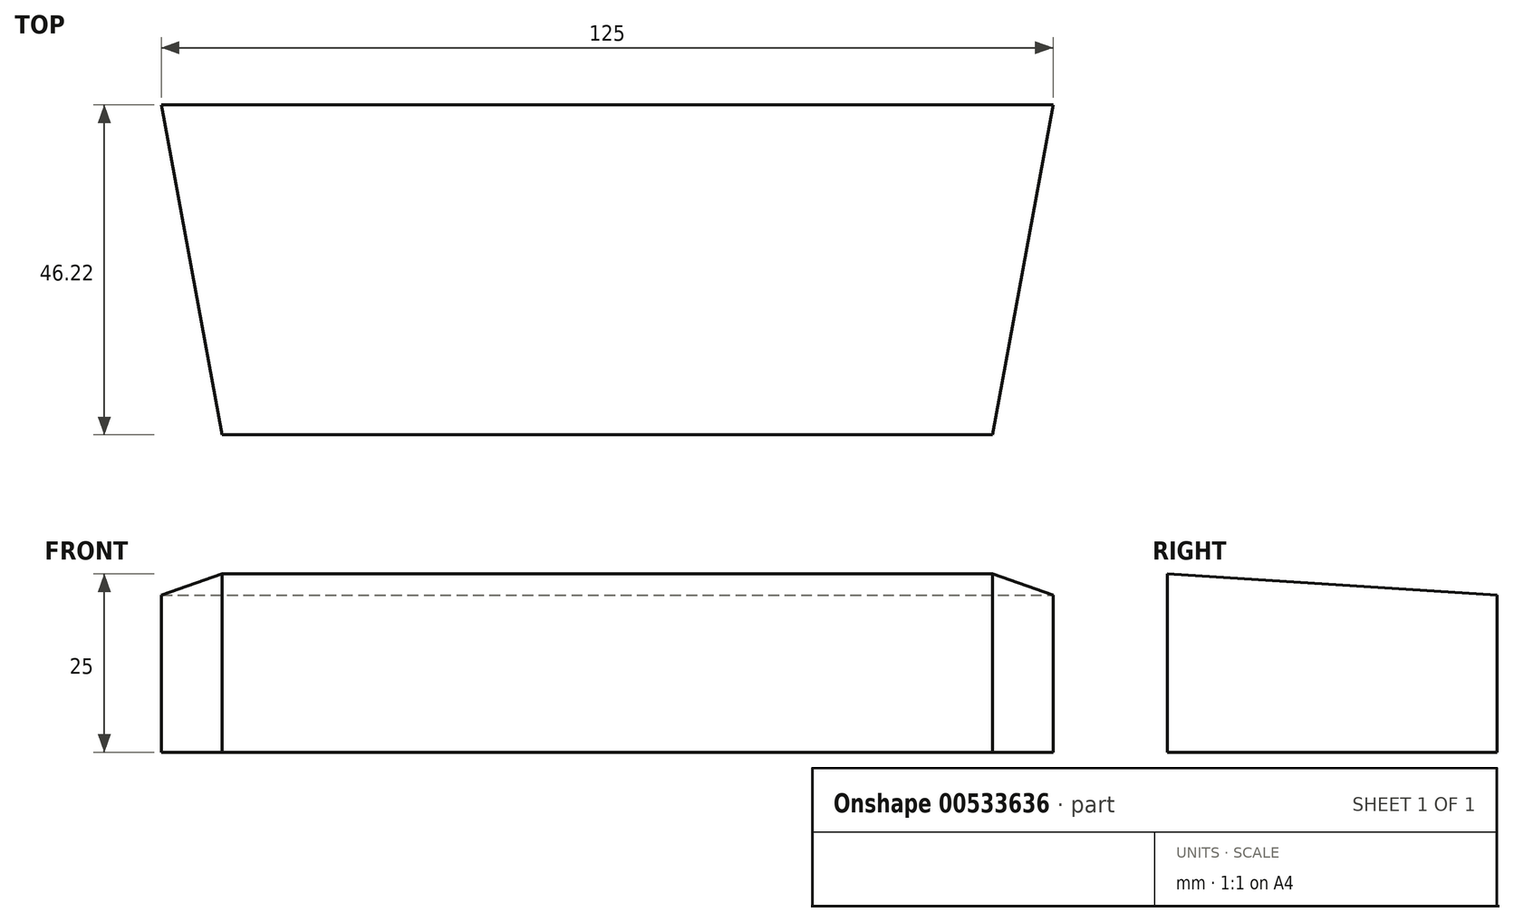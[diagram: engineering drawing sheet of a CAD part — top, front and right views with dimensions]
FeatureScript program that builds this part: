
annotation { "Feature Type Name" : "Feature", "Feature Type Description" : "" }
export const myFeature = defineFeature(function(context is Context, id is Id, definition is map)
    precondition{}
    {
        {
            var Q0;
            Q0=qCreatedBy(makeId("Top.planeOp"),FACE);
            var sketch = newSketch(context, id + "F0", { "sketchPlane" : qUnion([Q0])});
            skLineSegment(sketch, "E0", {"start": v(-54, 0) * mm, "end": v(54, 0) * mm});
            skLineSegment(sketch, "E1", {"start": v(54, 0) * mm, "end": v(62.5, 46.22) * mm});
            skLineSegment(sketch, "E2", {"start": v(62.5, 46.22) * mm, "end": v(-62.5, 46.22) * mm});
            skLineSegment(sketch, "E3", {"start": v(-62.5, 46.22) * mm, "end": v(-54, 0) * mm});
            skSolve(sketch);
        }
        {
            var Q0;
            Q0=makeQuery(id+"F0.imprint","IMPRINT",FACE,{"disambiguationData":[TD([[makeQuery(id+"F0.imprint","IMPRINT",EDGE,{"derivedFrom":sQuery(id+"F0.wireOp",EDGE,"E0")}),1.0]])]});
            extrude(context, id + "F1", {"entities" : qUnion([Q0]), "oppositeDirection" : true, "depth" : 25 * mm, "offsetDistance" : 25 * mm});
        }
        {
            var Q0;
            Q0=qCreatedBy(makeId("Right.planeOp"),FACE);
            var sketch = newSketch(context, id + "F2", { "sketchPlane" : qUnion([Q0])});
            skLineSegment(sketch, "E4", {"start": v(0, 0) * mm, "end": v(0, -25) * mm, "construction": true});
            skLineSegment(sketch, "E5", {"start": v(0, -25) * mm, "end": v(46.22, -25) * mm, "construction": true});
            skLineSegment(sketch, "E6", {"start": v(46.22, -25) * mm, "end": v(46.22, -3) * mm, "construction": true});
            skLineSegment(sketch, "E7", {"start": v(46.22, -3) * mm, "end": v(0, 0) * mm});
            skLineSegment(sketch, "E8", {"start": v(0, 0) * mm, "end": v(46.22, 0) * mm});
            skLineSegment(sketch, "E9", {"start": v(46.22, 0) * mm, "end": v(46.22, -3) * mm});
            skSolve(sketch);
        }
        {
            var Q0;
            Q0 = qSketchRegion(id + "F2", true);
            extrude(context, id + "F3", {"entities" : qUnion([Q0]), "operationType" : NewBodyOperationType.REMOVE, "endBound" : BoundingType.THROUGH_ALL, "oppositeDirection" : true, "depth" : 25 * mm, "offsetDistance" : 25 * mm, "hasSecondDirection" : true, "secondDirectionBound" : SecondDirectionBoundingType.THROUGH_ALL, "secondDirectionOppositeDirection" : false, "secondDirectionDepth" : 25 * mm});
        }
    });
